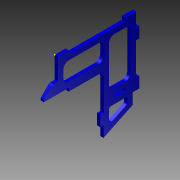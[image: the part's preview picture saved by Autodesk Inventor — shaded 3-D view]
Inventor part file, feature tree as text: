
AUTODESK INVENTOR PART (.ipt)
format: ipt  version: 2012 (Build 160160000, 160)  size: 183,296 bytes
history: native  units: mm
features: sketch x2, extrude x1
ambient origin geometry x8: Origin, YZ Plane, XZ Plane, XY Plane, X Axis, Y Axis, Z Axis, Center Point
feature tree (3):
  sketch  "Sketch1"  dims[d4=10.0mm d5=52.0mm]
  extrude  "Extrusion5"  Depth=52.0mm
  sketch  "Sketch2"  dims[d6=10.0mm d8=10.0mm d11=3.0mm d15=3.0mm d29=10.0mm d33=5.0mm d36=5.0mm d40=5.0mm d46=30.0mm d47=3.0mm d48=10.0mm d50=3.0mm d53=42.0mm d55=10.0mm d57=3.0mm d59=5.0mm d60=5.0mm d61=5.0mm d62=10.0mm d63=3.0mm d64=10.0mm d67=53.0mm d68=27.0mm d69=5.0mm d75=90.0deg d76=90.0deg d77=90.0deg d78=3.0mm d79=90.0deg d80=6.0mm d81=30.000027mm d82=27.0mm d83=10.0mm d84=10.0mm d85=3.0mm d86=3.0mm d87=30.0mm d90=5.0mm d91=13.0mm d92=33.0mm d95=2.0mm d97=5.0mm d98=5.0mm d99=5.0mm d100=5.0mm d101=2.0mm d102=3.0mm d103=0.0mm d104=5.0mm d105=5.0mm d106=8.0mm d107=33.0mm d108=23.0mm d109=3.0mm d110=2.0mm d111=10.0mm]
